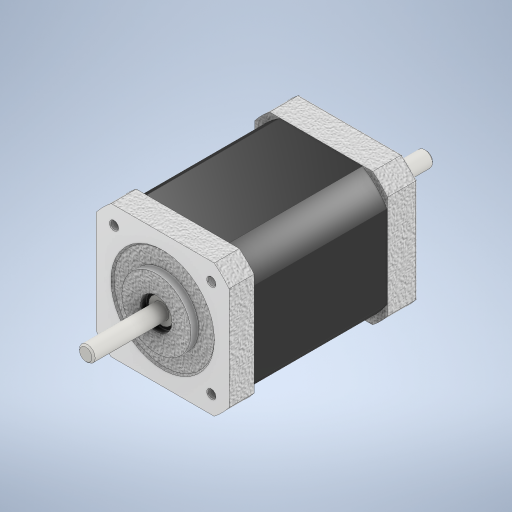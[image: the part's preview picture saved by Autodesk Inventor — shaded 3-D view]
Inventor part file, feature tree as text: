
AUTODESK INVENTOR PART (.ipt)
format: ipt  version: 2024 (Build 280153000, 153)  size: 588,800 bytes
history: native  units: mm
features: extrude x14, projected_geometry x7, plane x4, chamfer x4, hole x2, fillet x2, pattern_circular x1, sketch x1
ambient origin geometry x8: Origin, YZ Plane, XZ Plane, XY Plane, X Axis, Y Axis, Z Axis, Center Point
bodies: Solid1 (feature_tree)
feature tree (35):
  extrude  "Extrusion1"  Depth=42.3mm
  extrude  "Extrusion2"  Depth=2.0mm
  hole  "Hole1"  [1 undecoded]
  plane  "Work Plane1"
  extrude  "Extrusion3"  Depth=2.0mm
  extrude  "Extrusion5"  Depth=2.0mm
  chamfer  "Chamfer1"  Distance=8.0mm
  hole  "Hole2"  [1 undecoded]
  plane  "Work Plane2"
  extrude  "Extrusion6"  [1 undecoded]
  chamfer  "Chamfer2"  Distance=9.5mm
  extrude  "Extrusion7"  Depth=2.0mm
  extrude  "Extrusion8"  Depth=0.1mm
  extrude  "Extrusion9"  Depth=10.0mm TaperAngle=0.0deg
  plane  "Work Plane4"
  extrude  "Extrusion10"  Depth=0.25mm TaperAngle=45.0deg
  plane  "Work Plane5"
  chamfer  "Chamfer5"  Distance=5.0mm
  extrude  "Extrusion15"  Depth=8.0mm
  extrude  "Extrusion11"  Depth=10.0mm TaperAngle=0.0deg
  extrude  "Extrusion13"  Depth=4.5mm
  fillet  "Fillet3"  Radius=0.5mm
  extrude  "Extrusion12"  Depth=2.0mm TaperAngle=0.0deg
  fillet  "Fillet1"  Radius=0.5mm
  pattern_circular  "Circular Pattern2"  [2 undecoded]
  extrude  "Extrusion14"  Depth=2.0mm TaperAngle=0.0deg
  chamfer  "Chamfer4"  Distance=8.0mm
  projected_geometry  "Projected Loop1"
  projected_geometry  "Projected Loop2"
  projected_geometry  "Projected Loop3"
  projected_geometry  "Projected Loop5"
  projected_geometry  "Projected Loop6"
  projected_geometry  "Projected Loop7"
  sketch  "Sketch11"  dims[d0=42.3mm d1=42.3mm d2=31.0mm d3=31.0mm d4=49.9mm d5=22.0mm d6=8.0mm d7=0.0mm d8=2.0mm d9=0.0mm d10=2.459mm d11=6.0mm d12=8.0mm d13=4.1mm d14=90.0deg d15=4.5mm d16=0.0mm d17=-60.0mm d18=9.5mm d19=0.0mm d20=49.85mm d23=0.1mm d24=10.0mm d25=0.0mm d26=0.25mm d27=2.0mm d28=45.0deg d29=10.0mm d30=6.0mm d31=8.0mm d32=4.1mm d33=90.0deg d34=2.0mm d35=0.0mm d36=5.0mm d37=8.0mm d38=24.5mm d39=10.0mm d40=0.0mm d41=4.5mm d42=0.5mm d43=2.0mm d44=45.0deg d45=22.298mm d46=0.0mm d47=0.5mm d48=0.0mm d49=10.0mm d50=3.0mm d51=0.0mm d52=8.0mm d53=5.0mm d54=1.0mm d55=0.0mm d56=0.5mm d57=0.0mm d69=2.0mm d70=0.0mm d71=0.5mm d72=24.5mm d73=2.0mm d74=0.0mm d79=0.5mm d80=5.5mm d81=40.0mm d82=360.0deg d84=32.0mm d85=0.5mm d86=0.0mm d87=0.5mm d88=2.0mm d89=45.0deg d90=53.55mm d92=24.0mm d93=-15.0mm d94=2.0mm d95=0.0mm d96=0.0mm d97=0.5mm d98=2.0mm d99=45.0deg]
  projected_geometry  "Project Cut Edges1"
note: 5 required parameter values undecoded (feature->parameter linkage not recoverable at this tier; creation-order binding heuristic only, values carry confidence <= 0.55)
